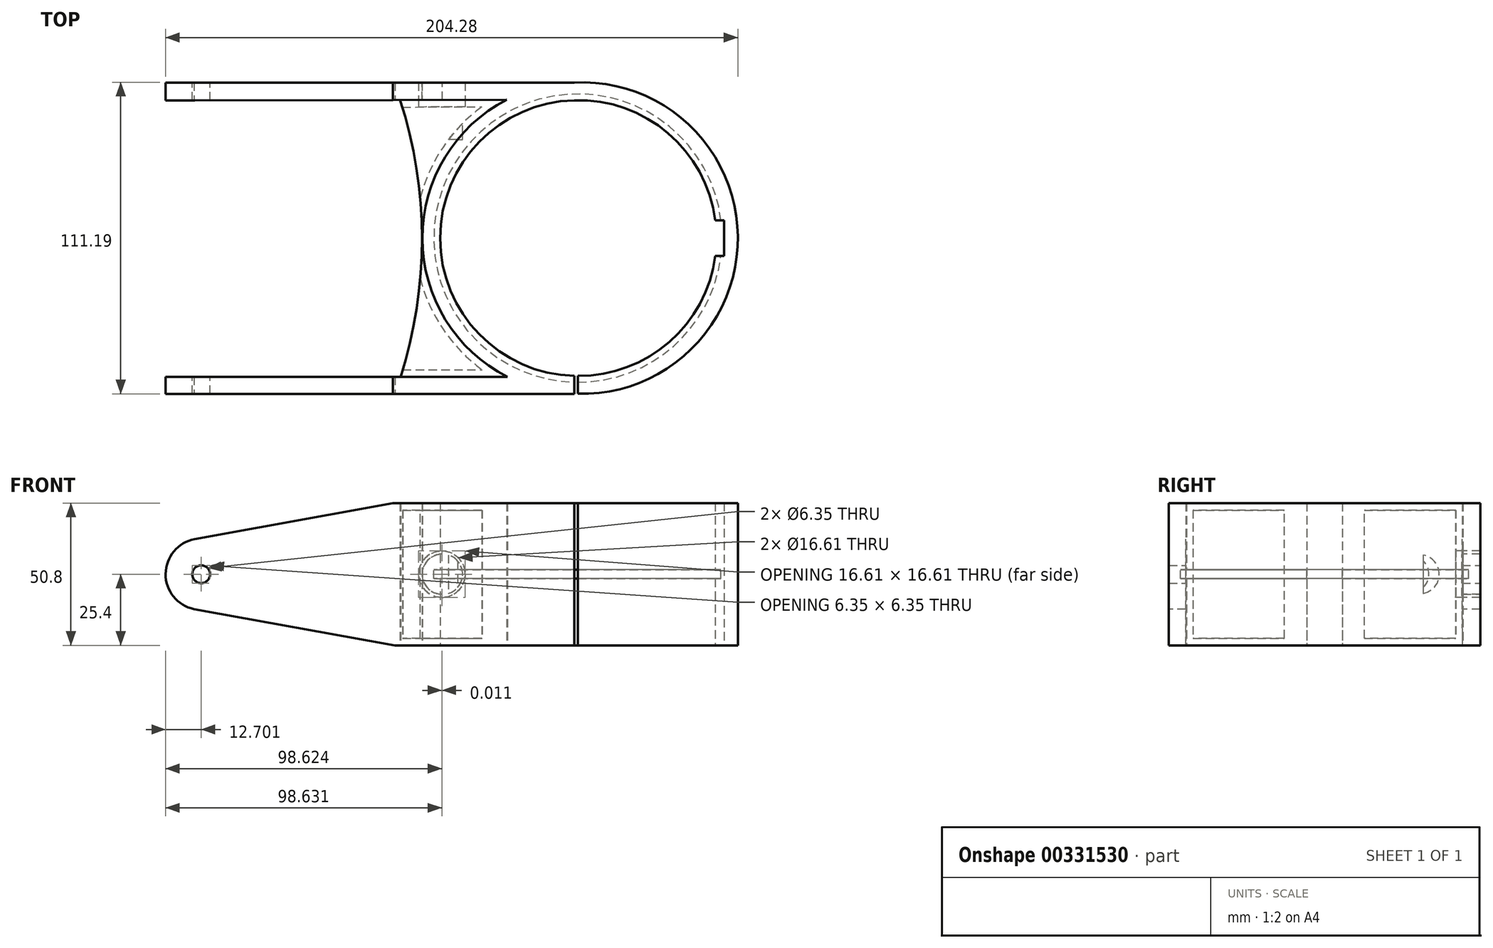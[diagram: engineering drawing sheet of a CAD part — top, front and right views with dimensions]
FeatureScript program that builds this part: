
annotation { "Feature Type Name" : "Feature", "Feature Type Description" : "" }
export const myFeature = defineFeature(function(context is Context, id is Id, definition is map)
    precondition{}
    {
        {
            var Q0;
            Q0=qCreatedBy(makeId("Top.planeOp"),FACE);
            var sketch = newSketch(context, id + "F0", { "sketchPlane" : qUnion([Q0])});
            skArc(sketch, "E0", {"start": v(0, -49.21) * mm, "mid": v(0.63, 49.2) * mm, "end": v(-1.27, -49.2) * mm});
            skArc(sketch, "E1.0", {"start": v(-25.41, 49.4) * mm, "mid": v(-55.56, -0.1) * mm, "end": v(-25.23, -49.5) * mm});
            skLineSegment(sketch, "E2", {"start": v(-1.27, 55.55) * mm, "end": v(-1.27, 49.2) * mm});
            skLineSegment(sketch, "E3", {"start": v(0, -49.21) * mm, "end": v(0, -55.56) * mm});
            skLineSegment(sketch, "E4.bottom", {"start": v(-1.27, 55.55) * mm, "end": v(-147.32, 55.55) * mm});
            skLineSegment(sketch, "E4.top", {"start": v(-1.27, -55.58) * mm, "end": v(-147.32, -55.58) * mm});
            skLineSegment(sketch, "E5.trimOffspring", {"start": v(-1.27, -49.2) * mm, "end": v(-1.27, -55.58) * mm});
            skLineSegment(sketch, "E6", {"start": v(-147.32, 55.55) * mm, "end": v(-147.32, 49.1) * mm});
            skLineSegment(sketch, "E7", {"start": v(-147.32, -55.58) * mm, "end": v(-147.32, -49.5) * mm});
            skLineSegment(sketch, "E8", {"start": v(-147.32, -49.5) * mm, "end": v(-25.23, -49.5) * mm});
            skLineSegment(sketch, "E9", {"start": v(-147.32, 49.1) * mm, "end": v(-25.41, 49.4) * mm});
            skArc(sketch, "E10", {"start": v(-63.33, -49.5) * mm, "mid": v(-55.7, -0.03) * mm, "end": v(-63.51, 49.4) * mm});
            skLineSegment(sketch, "E11", {"start": v(-69.68, -49.5) * mm, "end": v(-63.33, -49.5) * mm});
            skArc(sketch, "E12", {"start": v(0, -55.56) * mm, "mid": v(57.05, 0.65) * mm, "end": v(-1.27, 55.55) * mm});
            skArc(sketch, "E13", {"start": v(0, -49.21) * mm, "mid": v(49.45, 0.64) * mm, "end": v(-1.27, 49.2) * mm});
            skLineSegment(sketch, "E14", {"start": v(49.04, 6.35) * mm, "end": v(52.21, 6.35) * mm});
            skLineSegment(sketch, "E15", {"start": v(52.21, 6.35) * mm, "end": v(52.21, -6.35) * mm});
            skLineSegment(sketch, "E16", {"start": v(52.21, -6.35) * mm, "end": v(49.04, -6.35) * mm});
            skSolve(sketch);
        }
        {
            var Q0;
            {var subQ3=sQuery(id+"F0.wireOp",EDGE,"E4.bottom");Q0=makeQuery(id+"F0.imprint","IMPRINT",FACE,{"disambiguationData":[TD([[makeQuery(id+"F0.imprint","IMPRINT",EDGE,{"derivedFrom":subQ3}),1.0]])]});}
            var Q1;
            {var subQ2=sQuery(id+"F0.wireOp",EDGE,"E4.top");Q1=makeQuery(id+"F0.imprint","IMPRINT",FACE,{"disambiguationData":[TD([[makeQuery(id+"F0.imprint","IMPRINT",EDGE,{"derivedFrom":subQ2}),-1.0]])]});}
            var Q2;
            {var subQ4=sQuery(id+"F0.wireOp",EDGE,"E2");Q2=makeQuery(id+"F0.imprint","IMPRINT",FACE,{"disambiguationData":[TD([[makeQuery(id+"F0.imprint","IMPRINT",EDGE,{"derivedFrom":subQ4}),-1.0]])]});}
            extrude(context, id + "F1", {"entities" : qUnion([Q0, Q1, Q2]), "endBound" : BoundingType.SYMMETRIC, "depth" : 50.8 * mm});
        }
        {
            var Q0;
            Q0=makeQuery(id+"F1.opExtrude","SWEPT_FACE",FACE,{"disambiguationData":[OSD([sQuery(id+"F0.wireOp",EDGE,"E4.top")])]});
            var sketch = newSketch(context, id + "F2", { "sketchPlane" : qUnion([Q0])});
            skSolve(sketch);
        }
        {
            var Q0;
            {var subQ0=sQuery(id+"F0.wireOp",EDGE,"E1.0");Q0=makeQuery(id+"F0.imprint","IMPRINT",FACE,{"disambiguationData":[TD([[makeQuery(id+"F0.imprint","IMPRINT",EDGE,{"derivedFrom":subQ0}),-1.0]])]});}
            var Q1;
            Q1=sQuery(id+"F0.wireOp",EDGE,"E11");
            var Q2;
            Q2=sQuery(id+"F0.wireOp",EDGE,"E10");
            var Q3;
            Q3=sQuery(id+"F0.wireOp",EDGE,"rBlO6ro3-5g2z-FfBw-8hij-tyMhMfmKPz8U");
            var Q4;
            Q4=sQuery(id+"F0.wireOp",EDGE,"kr6a58jN-BYY1-x4jS-eH9u-tcZzHDnncJ3J");
            extrude(context, id + "F3", {"entities" : qUnion([Q0]), "surfaceEntities" : qUnion([Q1, Q2, Q3, Q4]), "endBound" : BoundingType.SYMMETRIC, "depth" : 50.8 * mm});
        }
        {
            var Q0;
            Q0=makeQuery(id+"F0.imprint","IMPRINT",FACE,{"disambiguationData":[TD([[makeQuery(id+"F0.imprint","IMPRINT",EDGE,{"derivedFrom":sQuery(id+"F0.wireOp",EDGE,"E12")}),1.0]])]});
            extrude(context, id + "F4", {"entities" : qUnion([Q0]), "operationType" : NewBodyOperationType.ADD, "endBound" : BoundingType.SYMMETRIC, "depth" : 50.8 * mm});
        }
        {
            var Q0;
            Q0=sQuery(id+"F0.wireOp",EDGE,"E16");
            var Q1;
            Q1=sQuery(id+"F0.wireOp",EDGE,"E14");
            var Q2;
            Q2=sQuery(id+"F0.wireOp",EDGE,"E15");
            extrude(context, id + "F5", {"bodyType" : ToolBodyType.SURFACE, "surfaceEntities" : qUnion([Q0, Q1, Q2]), "depth" : 25.4 * mm});
        }
        {
            var Q0;
            {var subQ0=sQuery(id+"F0.wireOp",EDGE,"E4.top");Q0=makeQuery(id+"F2.imprint","IMPRINT",FACE,{"disambiguationData":[TD([[makeQuery(id+"F2.imprint","IMPRINT",EDGE,{"derivedFrom":makeQuery(id+"F1.opExtrude","CAP_EDGE",EDGE,{"disambiguationData":[OSD([subQ0])],"isStart":true})}),-1.0]])]});}
            var sketch = newSketch(context, id + "F6", { "sketchPlane" : qUnion([Q0])});
            skArc(sketch, "E17", {"start": v(-136.8, 12.5) * mm, "mid": v(-147.22, 0.14) * mm, "end": v(-137.07, -12.44) * mm});
            skLineSegment(sketch, "E18", {"start": v(-136.8, 12.5) * mm, "end": v(-64.67, 25.67) * mm});
            skLineSegment(sketch, "E19.bottom", {"start": v(-147.4, -25.5) * mm, "end": v(-64.67, -25.5) * mm});
            skLineSegment(sketch, "E19.top", {"start": v(-147.4, 25.67) * mm, "end": v(-64.67, 25.67) * mm});
            skLineSegment(sketch, "E19.left", {"start": v(-147.4, -25.5) * mm, "end": v(-147.4, 25.67) * mm});
            skLineSegment(sketch, "E19.right", {"start": v(-64.67, -25.5) * mm, "end": v(-64.67, 25.67) * mm});
            skLineSegment(sketch, "E20", {"start": v(-137.07, -12.44) * mm, "end": v(-64.67, -25.5) * mm});
            skSolve(sketch);
        }
        {
            var Q0;
            {var subQ3=sQuery(id+"F6.wireOp",EDGE,"E17");Q0=makeQuery(id+"F6.imprint","IMPRINT",FACE,{"disambiguationData":[TD([[makeQuery(id+"F6.imprint","IMPRINT",EDGE,{"derivedFrom":subQ3}),-1.0]])]});}
            extrude(context, id + "F7", {"entities" : qUnion([Q0]), "operationType" : NewBodyOperationType.REMOVE, "depth" : -120.65 * mm});
        }
        {
            var Q0;
            Q0=makeQuery(id+"F1.opExtrude","SWEPT_FACE",FACE,{"disambiguationData":[OSD([sQuery(id+"F0.wireOp",EDGE,"E4.bottom")])]});
            var sketch = newSketch(context, id + "F8", { "sketchPlane" : qUnion([Q0])});
            skCircle(sketch, "E21", {"center": v(134.52, 0) * mm, "radius": 3.17 * mm});
            skSolve(sketch);
        }
        {
            var Q0;
            Q0=qSketchRegion(id+"F8",true);
            extrude(context, id + "F9", {"entities" : qUnion([Q0]), "operationType" : NewBodyOperationType.REMOVE, "oppositeDirection" : true, "depth" : 114.3 * mm});
        }
        {
            var Q0;
            Q0=qCreatedBy(makeId("Top.planeOp"),FACE);
            var sketch = newSketch(context, id + "F10", { "sketchPlane" : qUnion([Q0])});
            skCircle(sketch, "E22", {"center": v(0, 0) * mm, "radius": 51.46 * mm});
            skSolve(sketch);
        }
        {
            var Q0;
            Q0=qSketchRegion(id+"F10",true);
            extrude(context, id + "F11", {"entities" : qUnion([Q0]), "operationType" : NewBodyOperationType.REMOVE, "endBound" : BoundingType.SYMMETRIC, "oppositeDirection" : true, "depth" : 3.17 * mm});
        }
        {
            var Q0;
            Q0=makeQuery(id+"F3.opExtrude","SWEPT_FACE",FACE,{"disambiguationData":[OSD([sQuery(id+"F0.wireOp",EDGE,"E10")])]});
            shell(context, id + "F12", {"entities" : qUnion([Q0]), "thickness" : 2.54 * mm});
        }
        {
            var Q0;
            Q0=makeQuery(id+"F8.imprint","IMPRINT",FACE,{"disambiguationData":[TD([[makeQuery(id+"F8.imprint","IMPRINT",EDGE,{"derivedFrom":sQuery(id+"F8.wireOp",EDGE,"E21")}),-1.0]])]});
            var sketch = newSketch(context, id + "F13", { "sketchPlane" : qUnion([Q0])});
            skCircle(sketch, "E23", {"center": v(48.42, 0) * mm, "radius": 7.21 * mm});
            skSolve(sketch);
        }
        {
            var Q0;
            Q0=makeQuery(id+"F13.imprint","IMPRINT",FACE,{"disambiguationData":[TD([[makeQuery(id+"F13.imprint","IMPRINT",EDGE,{"derivedFrom":sQuery(id+"F13.wireOp",EDGE,"E23")}),1.0]])]});
            extrude(context, id + "F14", {"entities" : qUnion([Q0]), "operationType" : NewBodyOperationType.REMOVE, "oppositeDirection" : true, "depth" : 20.32 * mm});
        }
        {
            var Q0;
            Q0=makeQuery(id+"F12.opShell","OFFSET_FACE",FACE,{"disambiguationData":[OSD([sQuery(id+"F0.wireOp",EDGE,"E9")])]});
            var sketch = newSketch(context, id + "F15", { "sketchPlane" : qUnion([Q0])});
            skCircle(sketch, "E24", {"center": v(-48.45, 0) * mm, "radius": 8.3 * mm});
            skSolve(sketch);
        }
        {
            var Q0;
            Q0=makeQuery(id+"F15.imprint","IMPRINT",FACE,{"disambiguationData":[TD([[makeQuery(id+"F15.imprint","IMPRINT",EDGE,{"derivedFrom":sQuery(id+"F15.wireOp",EDGE,"E24")}),1.0]])]});
            extrude(context, id + "F16", {"entities" : qUnion([Q0]), "operationType" : NewBodyOperationType.REMOVE, "oppositeDirection" : true, "depth" : 17.78 * mm});
        }
    });
